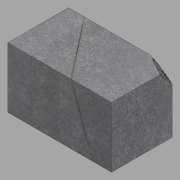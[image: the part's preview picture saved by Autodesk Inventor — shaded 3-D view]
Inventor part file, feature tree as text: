
AUTODESK INVENTOR PART (.ipt)
format: ipt  version: 2022.1 (Build 261234020, 234B)  size: 1,098,752 bytes
history: native  units: in
note: dims shown in document units (in); Inventor stores cm internally (conversion verified against a paired STEP export)
features: other x3, sketch x3, extrude x1, loft x1
ambient origin geometry x8: Origin, YZ Plane, XZ Plane, XY Plane, X Axis, Y Axis, Z Axis, Center Point
bodies: Solid1 (feature_tree)
feature tree (8):
  other  "2nd.ipt"
  extrude  "Extrusion1"  Depth=1.0in TaperAngle=0.0deg
  loft  "Loft1"
  other  "Solid1::2nd.ipt"
  other  "TaggingFeature1"
  sketch  "Sketch1"  dims[d0=0.3937in d1=1.0in d2=0.0in]
  sketch  "Sketch2"  dims[d3=0.0in d4=90.0deg d5=0.0in d6=90.0deg]
  sketch  "Sketch3"
